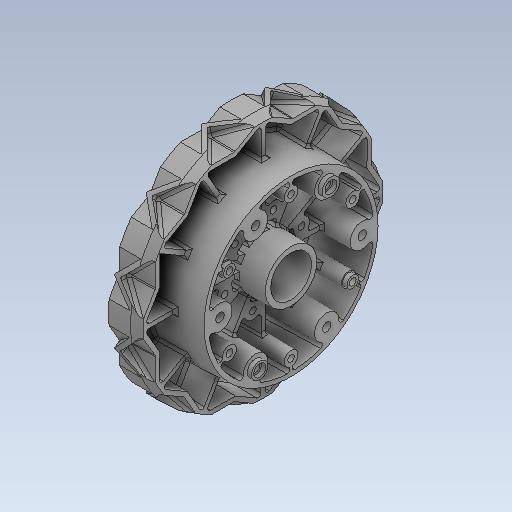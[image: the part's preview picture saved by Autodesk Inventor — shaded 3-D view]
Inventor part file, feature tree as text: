
AUTODESK INVENTOR PART (.ipt)
format: ipt  version: 2020.2 (Build 242310000, 310)  size: 2,868,224 bytes
history: native  units: in
note: dims shown in document units (in); Inventor stores cm internally (conversion verified against a paired STEP export)
features: fillet x1
ambient origin geometry x8: Origin, YZ Plane, XZ Plane, XY Plane, X Axis, Y Axis, Z Axis, Center Point
bodies: Solid1 (feature_tree)
feature tree (1):
  fillet  "Fillet141"  [1 undecoded]
note: 1 required parameter value undecoded (feature->parameter linkage not recoverable at this tier; creation-order binding heuristic only, values carry confidence <= 0.55)
